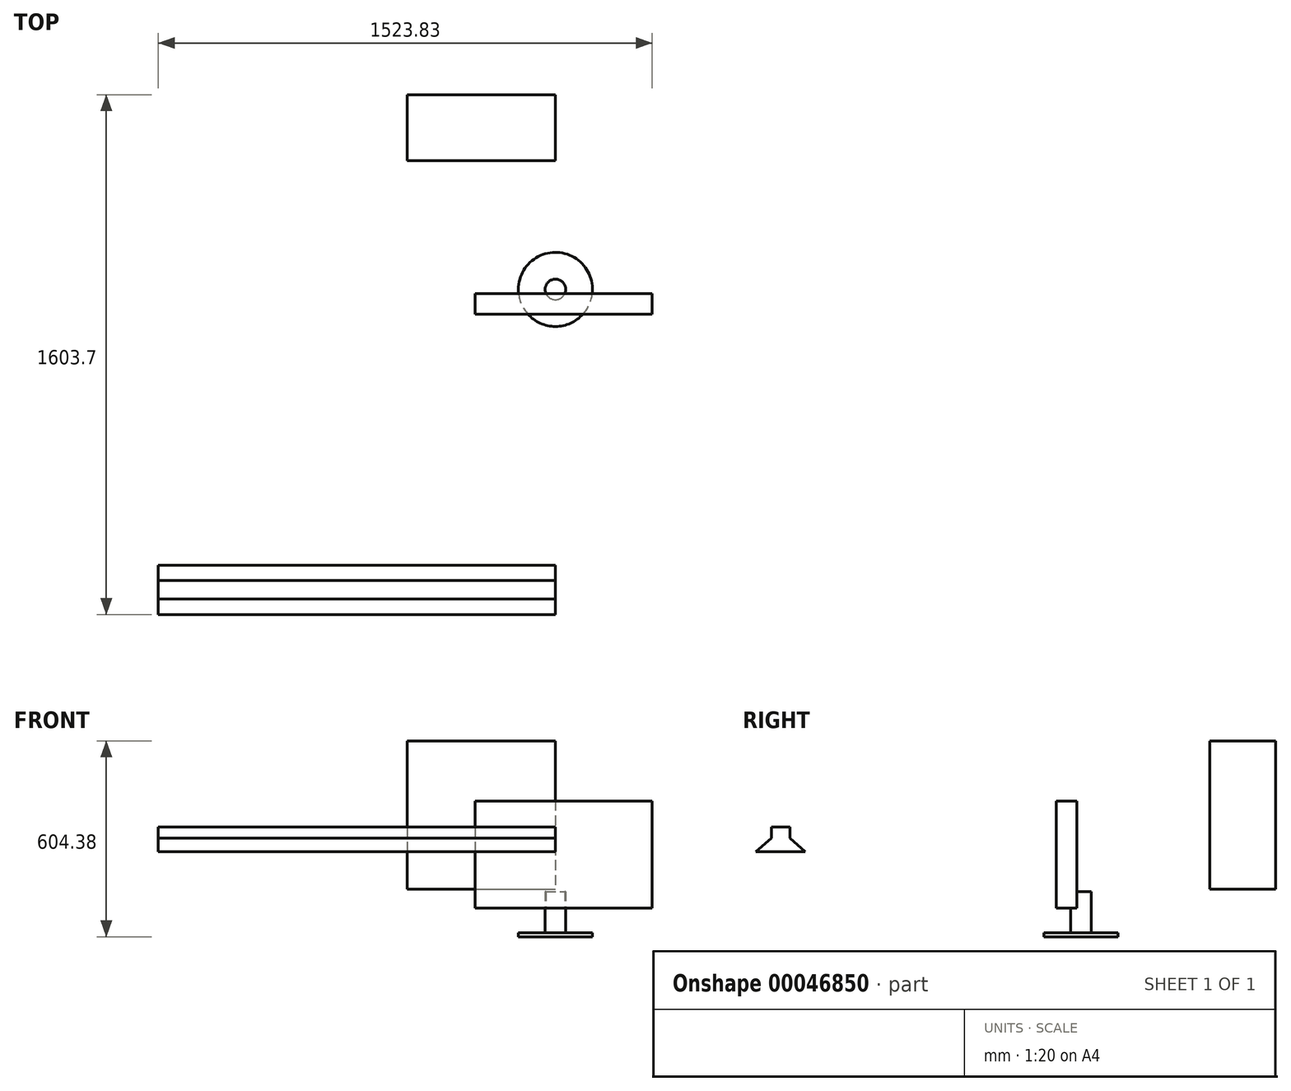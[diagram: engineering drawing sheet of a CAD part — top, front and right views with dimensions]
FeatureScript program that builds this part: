
annotation { "Feature Type Name" : "Feature", "Feature Type Description" : "" }
export const myFeature = defineFeature(function(context is Context, id is Id, definition is map)
    precondition{}
    {
        {
            var Q0;
            Q0=qCreatedBy(makeId("Front.planeOp"),FACE);
            var sketch = newSketch(context, id + "F0", { "sketchPlane" : qUnion([Q0])});
            skLineSegment(sketch, "E0.bottom", {"start": v(-247.82, 156.47) * mm, "end": v(298.28, 156.47) * mm});
            skLineSegment(sketch, "E0.top", {"start": v(-247.82, -173.73) * mm, "end": v(298.28, -173.73) * mm});
            skLineSegment(sketch, "E0.left", {"start": v(-247.82, 156.47) * mm, "end": v(-247.82, -173.73) * mm});
            skLineSegment(sketch, "E0.right", {"start": v(298.28, 156.47) * mm, "end": v(298.28, -173.73) * mm});
            skSolve(sketch);
        }
        {
            var Q0;
            Q0=qSketchRegion(id+"F0",true);
            extrude(context, id + "F1", {"entities" : qUnion([Q0]), "oppositeDirection" : true, "depth" : 63.5 * mm});
        }
        {
            var Q0;
            Q0=qCreatedBy(makeId("Right.planeOp"),FACE);
            var sketch = newSketch(context, id + "F2", { "sketchPlane" : qUnion([Q0])});
            skLineSegment(sketch, "E1", {"start": v(-774.57, 0) * mm, "end": v(-926.97, 0) * mm});
            skLineSegment(sketch, "E2", {"start": v(-926.97, 0) * mm, "end": v(-879.34, 41.27) * mm});
            skLineSegment(sketch, "E3", {"start": v(-879.34, 41.27) * mm, "end": v(-879.34, 76.2) * mm});
            skLineSegment(sketch, "E4", {"start": v(-879.34, 76.2) * mm, "end": v(-822.2, 76.2) * mm});
            skLineSegment(sketch, "E5", {"start": v(-822.2, 76.2) * mm, "end": v(-822.2, 41.27) * mm});
            skLineSegment(sketch, "E6", {"start": v(-822.2, 41.28) * mm, "end": v(-774.57, 0) * mm});
            skLineSegment(sketch, "E7", {"start": v(-850.77, 95.44) * mm, "end": v(-850.77, 0) * mm, "construction": true});
            skPoint(sketch, "E7.startSnap0", {"position": v(-850.77, 76.2) * mm});
            skSolve(sketch);
        }
        {
            var Q0;
            Q0=qSketchRegion(id+"F2",true);
            extrude(context, id + "F3", {"entities" : qUnion([Q0]), "oppositeDirection" : true, "depth" : 1225.55 * mm});
        }
        {
            var Q0;
            Q0=makeQuery(id+"F1.opExtrude","SWEPT_FACE",FACE,{"disambiguationData":[OSD([sQuery(id+"F0.wireOp",EDGE,"E0.top")])]});
            var sketch = newSketch(context, id + "F4", { "sketchPlane" : qUnion([Q0])});
            skCircle(sketch, "E8", {"center": v(0, -76.2) * mm, "radius": 31.75 * mm});
            skSolve(sketch);
        }
        {
            var Q0;
            Q0=qSketchRegion(id+"F4",true);
            extrude(context, id + "F5", {"entities" : qUnion([Q0]), "operationType" : NewBodyOperationType.ADD, "oppositeDirection" : true, "depth" : 50.8 * mm, "hasSecondDirection" : true, "secondDirectionOppositeDirection" : false, "secondDirectionDepth" : 88.9 * mm});
        }
        {
            var Q0;
            Q0=makeQuery(id+"F5.opExtrude","CAP_FACE",FACE,{"disambiguationData":[OSD([sQuery(id+"F4.wireOp",EDGE,"E8")])],"isStart":true});
            var sketch = newSketch(context, id + "F6", { "sketchPlane" : qUnion([Q0])});
            skCircle(sketch, "E9", {"center": v(0, -76.2) * mm, "radius": 114.3 * mm});
            skSolve(sketch);
        }
        {
            var Q0;
            Q0=makeQuery(id+"F6.imprint","IMPRINT",FACE,{"disambiguationData":[TD([[makeQuery(id+"F6.imprint","IMPRINT",EDGE,{"derivedFrom":sQuery(id+"F6.wireOp",EDGE,"E9")}),1.0]])]});
            extrude(context, id + "F7", {"entities" : qUnion([Q0]), "operationType" : NewBodyOperationType.ADD, "oppositeDirection" : true, "depth" : 12.7 * mm});
        }
        {
            var Q0;
            Q0=qCreatedBy(makeId("Right.planeOp"),FACE);
            var sketch = newSketch(context, id + "F8", { "sketchPlane" : qUnion([Q0])});
            skLineSegment(sketch, "E10.bottom", {"start": v(473.53, 341.75) * mm, "end": v(676.73, 341.75) * mm});
            skLineSegment(sketch, "E10.top", {"start": v(473.53, -115.45) * mm, "end": v(676.73, -115.45) * mm});
            skLineSegment(sketch, "E10.left", {"start": v(473.53, 341.75) * mm, "end": v(473.53, -115.45) * mm});
            skLineSegment(sketch, "E10.right", {"start": v(676.73, 341.75) * mm, "end": v(676.73, -115.45) * mm});
            skSolve(sketch);
        }
        {
            var Q0;
            Q0=makeQuery(id+"F8.imprint","IMPRINT",FACE,{"disambiguationData":[TD([[makeQuery(id+"F8.imprint","IMPRINT",EDGE,{"derivedFrom":sQuery(id+"F8.wireOp",EDGE,"E10.bottom")}),-1.0]])]});
            extrude(context, id + "F9", {"entities" : qUnion([Q0]), "oppositeDirection" : true, "depth" : 457.2 * mm});
        }
    });
